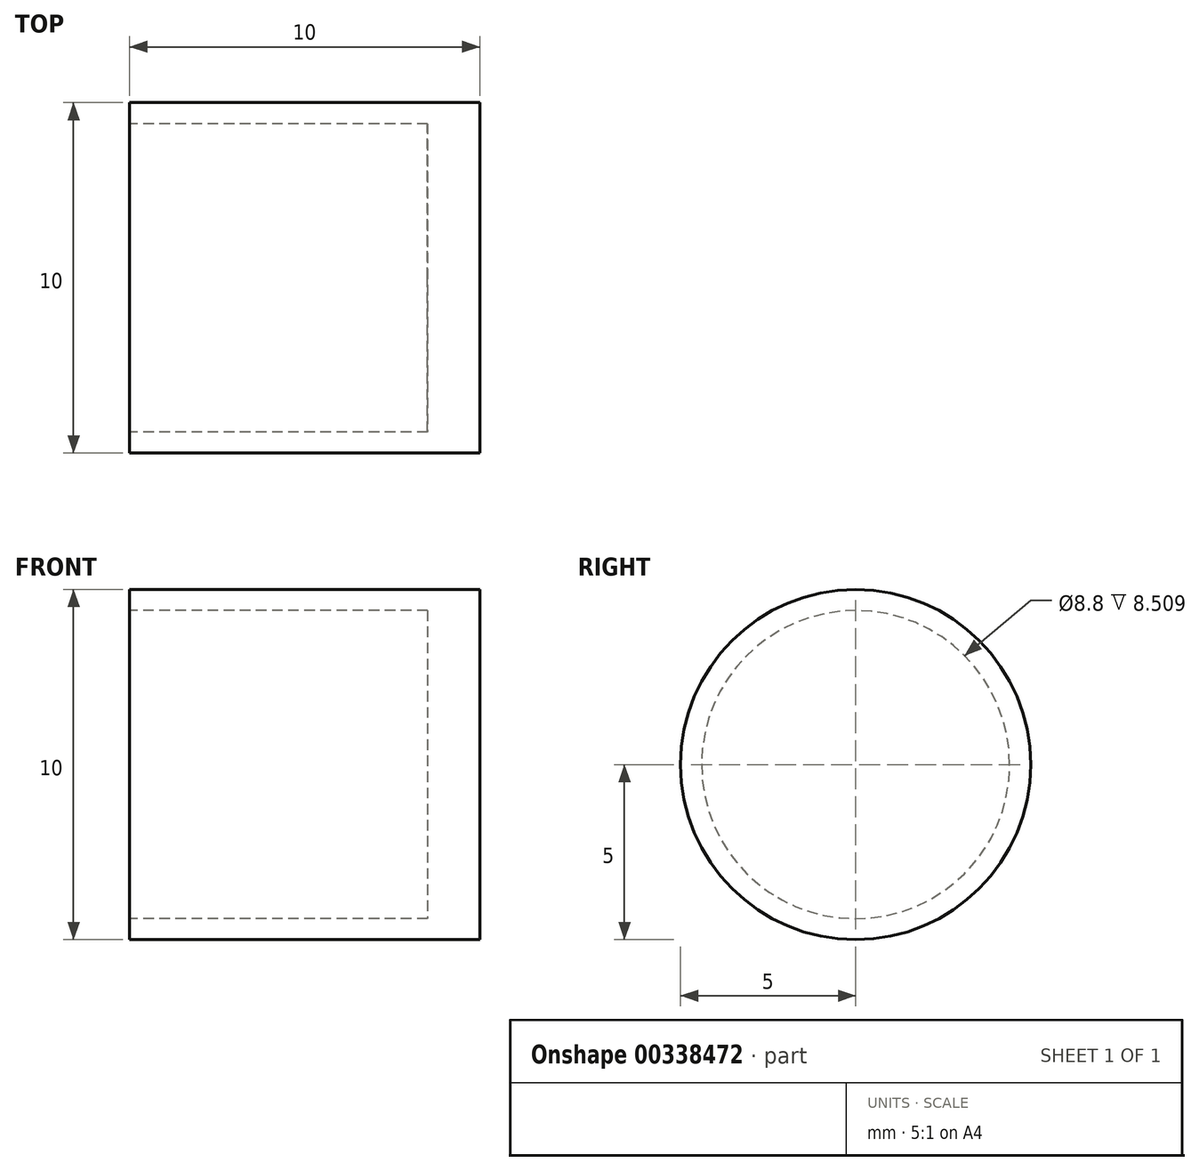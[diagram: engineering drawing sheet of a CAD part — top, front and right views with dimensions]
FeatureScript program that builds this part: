
annotation { "Feature Type Name" : "Feature", "Feature Type Description" : "" }
export const myFeature = defineFeature(function(context is Context, id is Id, definition is map)
    precondition{}
    {
        {
            var Q0;
            Q0=qCreatedBy(makeId("Front.planeOp"),FACE);
            var sketch = newSketch(context, id + "F0", { "sketchPlane" : qUnion([Q0])});
            skLineSegment(sketch, "E0", {"start": v(-10, 5) * mm, "end": v(0, 5) * mm});
            skLineSegment(sketch, "E1", {"start": v(0, 5) * mm, "end": v(0, 0) * mm});
            skLineSegment(sketch, "E2", {"start": v(-10, 0) * mm, "end": v(0, 0) * mm});
            skLineSegment(sketch, "E3", {"start": v(-10, 5) * mm, "end": v(-10, 0) * mm});
            skLineSegment(sketch, "E4", {"start": v(-10, 0) * mm, "end": v(0, 0) * mm, "construction": true});
            skSolve(sketch);
        }
        {
            var Q0;
            Q0 = qSketchRegion(id + "F0", true);
            var Q1;
            Q1=sQuery(id+"F0.wireOp",EDGE,"E2");
            revolve(context, id + "F1", {"entities" : qUnion([Q0]), "axis" : qUnion([Q1]), "revolveType" : RevolveType.FULL});
        }
        {
            var Q0;
            Q0=makeQuery(id+"F1.opRevolve","SWEPT_FACE",FACE,{"disambiguationData":[OSD([sQuery(id+"F0.wireOp",EDGE,"E3")])]});
            var sketch = newSketch(context, id + "F2", { "sketchPlane" : qUnion([Q0])});
            skCircle(sketch, "E5", {"center": v(0, 0) * mm, "radius": 4.4 * mm});
            skSolve(sketch);
        }
        {
            var Q0;
            Q0 = qSketchRegion(id + "F2", true);
            extrude(context, id + "F3", {"entities" : qUnion([Q0]), "operationType" : NewBodyOperationType.REMOVE, "oppositeDirection" : true, "depth" : 8.5 * mm});
        }
    });
